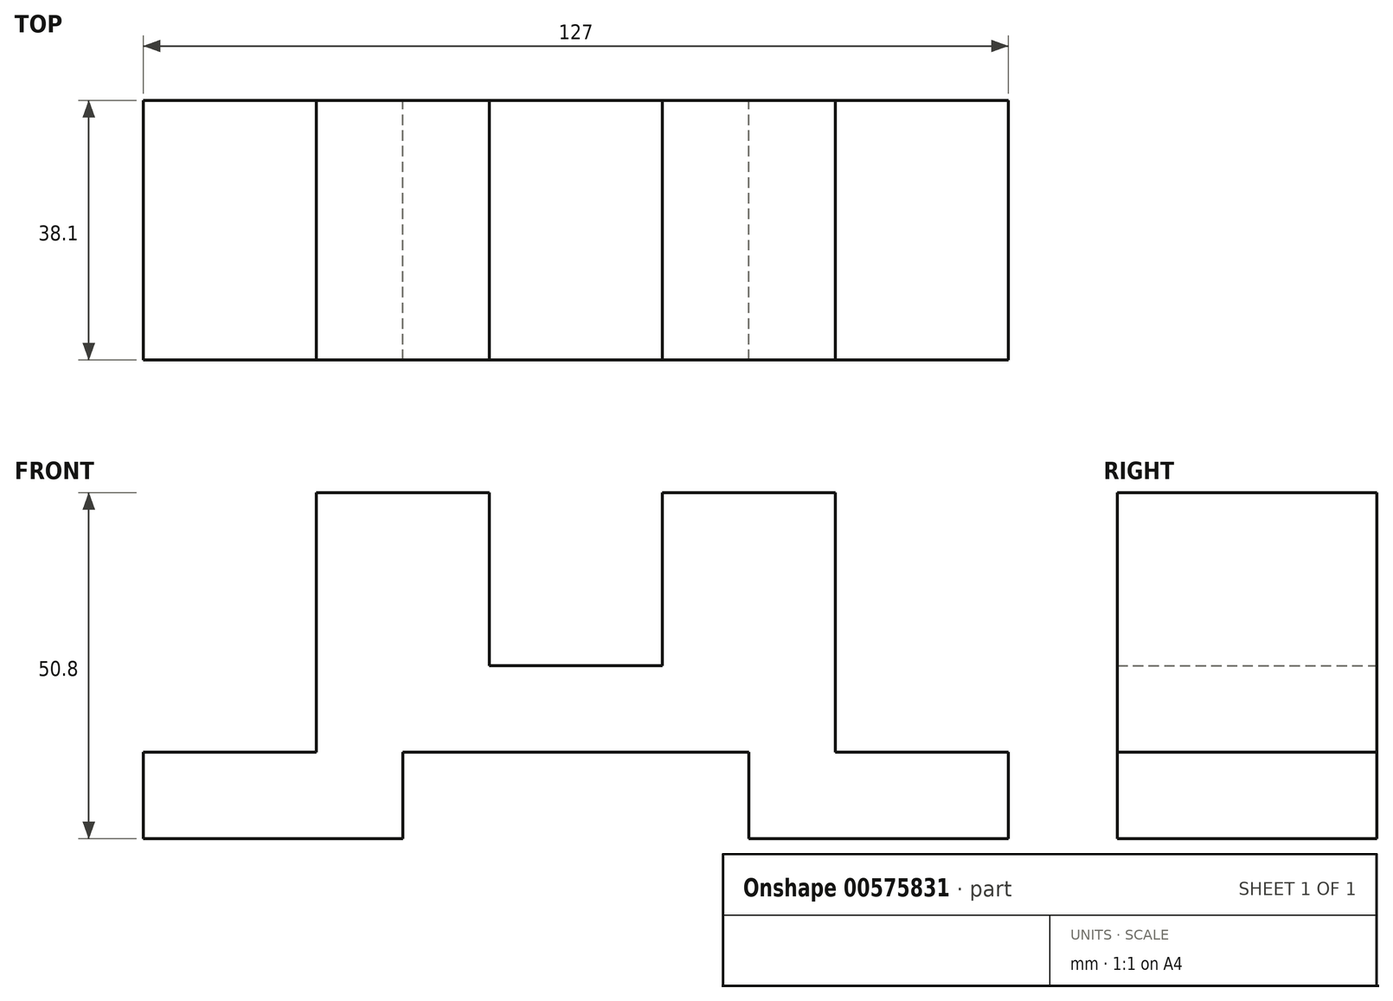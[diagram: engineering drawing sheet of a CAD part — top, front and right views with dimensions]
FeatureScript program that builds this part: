
annotation { "Feature Type Name" : "Feature", "Feature Type Description" : "" }
export const myFeature = defineFeature(function(context is Context, id is Id, definition is map)
    precondition{}
    {
        {
            var Q0;
            Q0=qCreatedBy(makeId("Front.planeOp"),FACE);
            var sketch = newSketch(context, id + "F0", { "sketchPlane" : qUnion([Q0])});
            skLineSegment(sketch, "E0", {"start": v(-75.49, -43.02) * mm, "end": v(-75.49, -55.72) * mm});
            skLineSegment(sketch, "E1", {"start": v(-75.49, -43.02) * mm, "end": v(-50.09, -43.02) * mm});
            skLineSegment(sketch, "E2", {"start": v(-50.09, -43.02) * mm, "end": v(-50.09, -4.92) * mm});
            skLineSegment(sketch, "E3", {"start": v(-50.09, -4.92) * mm, "end": v(-24.69, -4.92) * mm});
            skLineSegment(sketch, "E4", {"start": v(-24.69, -4.92) * mm, "end": v(-24.69, -30.32) * mm});
            skLineSegment(sketch, "E5", {"start": v(-24.69, -30.32) * mm, "end": v(0.71, -30.32) * mm});
            skLineSegment(sketch, "E6", {"start": v(0.71, -30.32) * mm, "end": v(0.71, -4.92) * mm});
            skLineSegment(sketch, "E7", {"start": v(0.71, -4.92) * mm, "end": v(26.11, -4.92) * mm});
            skPoint(sketch, "E8.end.orphan", {"position": v(27.02, -30.32) * mm});
            skLineSegment(sketch, "E9", {"start": v(26.11, -4.92) * mm, "end": v(26.11, -43.02) * mm});
            skLineSegment(sketch, "E10", {"start": v(26.11, -43.02) * mm, "end": v(51.51, -43.02) * mm});
            skLineSegment(sketch, "E11", {"start": v(51.51, -43.02) * mm, "end": v(51.51, -55.72) * mm});
            skLineSegment(sketch, "E12", {"start": v(-75.49, -55.72) * mm, "end": v(-37.39, -55.72) * mm});
            skLineSegment(sketch, "E13", {"start": v(51.51, -55.72) * mm, "end": v(13.41, -55.72) * mm});
            skLineSegment(sketch, "E14", {"start": v(-37.39, -55.72) * mm, "end": v(-37.39, -43.02) * mm});
            skLineSegment(sketch, "E15", {"start": v(13.41, -55.72) * mm, "end": v(13.41, -43.02) * mm});
            skLineSegment(sketch, "E16", {"start": v(-37.39, -43.02) * mm, "end": v(13.41, -43.02) * mm});
            skSolve(sketch);
        }
        {
            var Q0;
            Q0 = qSketchRegion(id + "F0", true);
            extrude(context, id + "F1", {"entities" : qUnion([Q0]), "depth" : 38.1 * mm, "offsetDistance" : 25.4 * mm});
        }
    });
